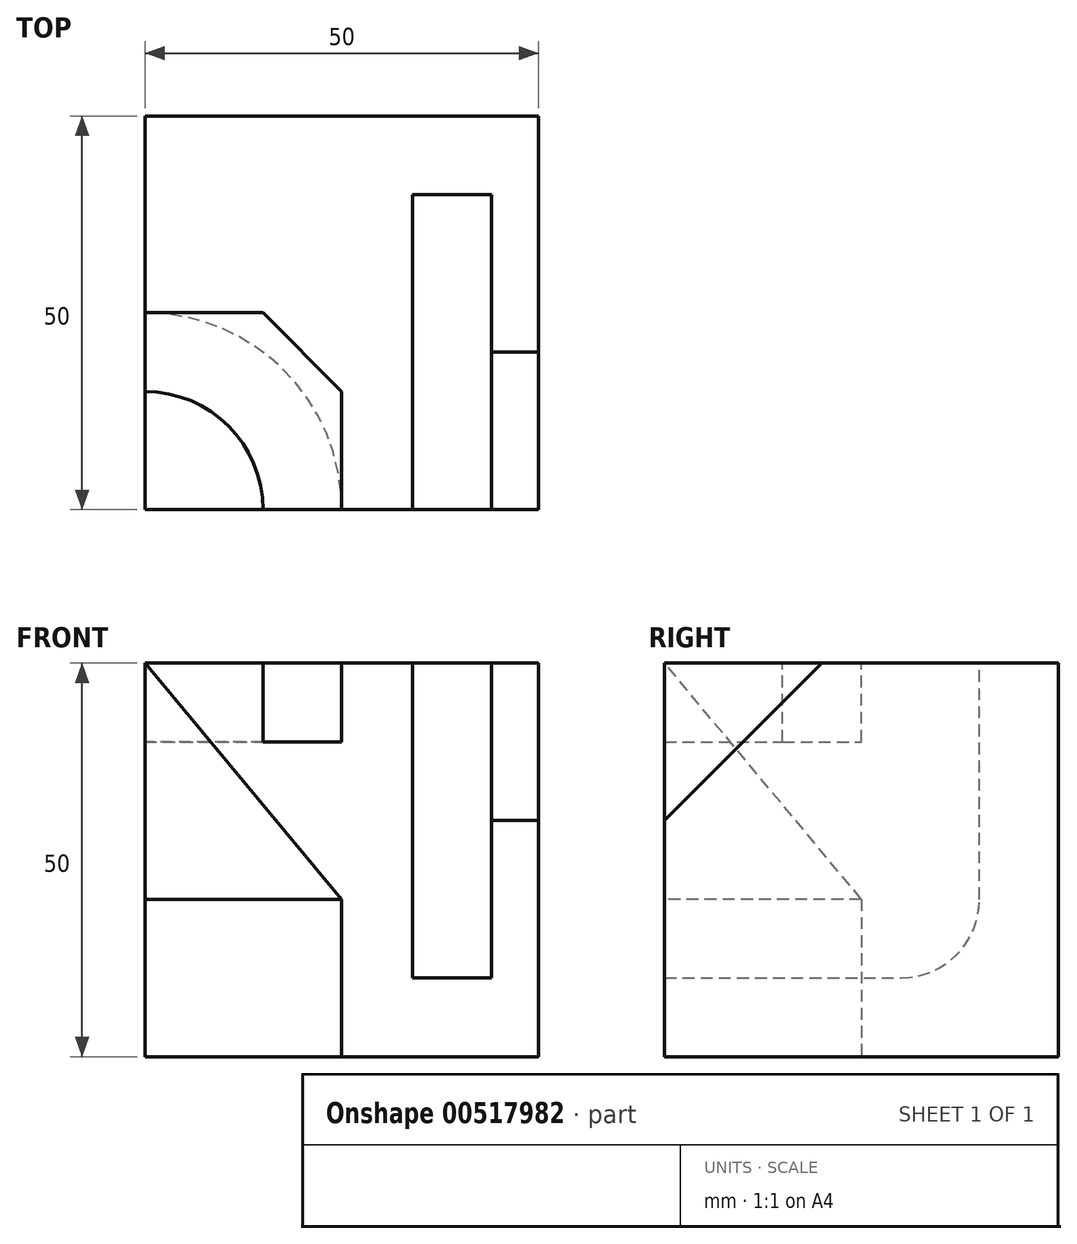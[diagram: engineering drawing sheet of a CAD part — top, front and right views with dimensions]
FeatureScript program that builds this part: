
annotation { "Feature Type Name" : "Feature", "Feature Type Description" : "" }
export const myFeature = defineFeature(function(context is Context, id is Id, definition is map)
    precondition{}
    {
        {
            var Q0;
            Q0=qCreatedBy(makeId("Top.planeOp"),FACE);
            var sketch = newSketch(context, id + "F0", { "sketchPlane" : qUnion([Q0])});
            skLineSegment(sketch, "E0.bottom", {"start": v(0, 0) * mm, "end": v(50, 0) * mm});
            skLineSegment(sketch, "E0.top", {"start": v(0, 50) * mm, "end": v(50, 50) * mm});
            skLineSegment(sketch, "E0.left", {"start": v(0, 0) * mm, "end": v(0, 50) * mm});
            skLineSegment(sketch, "E0.right", {"start": v(50, 0) * mm, "end": v(50, 50) * mm});
            skSolve(sketch);
        }
        {
            var Q0;
            Q0 = qSketchRegion(id + "F0", true);
            extrude(context, id + "F1", {"entities" : qUnion([Q0]), "depth" : 50 * mm, "offsetDistance" : 25 * mm});
        }
        {
            var Q0;
            Q0=makeQuery(id+"F1.opExtrude","CAP_FACE",FACE,{"disambiguationData":[OSD([sQuery(id+"F0.wireOp",EDGE,"E0.bottom"),sQuery(id+"F0.wireOp",EDGE,"E0.top"),sQuery(id+"F0.wireOp",EDGE,"E0.left"),sQuery(id+"F0.wireOp",EDGE,"E0.right")])],"isStart":false});
            var sketch = newSketch(context, id + "F2", { "sketchPlane" : qUnion([Q0])});
            skLineSegment(sketch, "E1.bottom", {"start": v(34, 0) * mm, "end": v(44, 0) * mm});
            skLineSegment(sketch, "E1.top", {"start": v(34, 40) * mm, "end": v(44, 40) * mm});
            skLineSegment(sketch, "E1.left", {"start": v(34, 0) * mm, "end": v(34, 40) * mm});
            skLineSegment(sketch, "E1.right", {"start": v(44, 0) * mm, "end": v(44, 40) * mm});
            skSolve(sketch);
        }
        {
            var Q0;
            Q0 = qSketchRegion(id + "F2", true);
            extrude(context, id + "F3", {"entities" : qUnion([Q0]), "operationType" : NewBodyOperationType.REMOVE, "oppositeDirection" : true, "depth" : 40 * mm, "offsetDistance" : 25 * mm});
        }
        {
            var Q0;
            Q0=makeQuery(id+"F1.opExtrude","SWEPT_FACE",FACE,{"disambiguationData":[OSD([sQuery(id+"F0.wireOp",EDGE,"E0.bottom")])]});
            var sketch = newSketch(context, id + "F4", { "sketchPlane" : qUnion([Q0])});
            skLineSegment(sketch, "E2", {"start": v(44, 30) * mm, "end": v(50, 30) * mm});
            skSolve(sketch);
        }
        {
            var Q0;
            Q0=makeQuery(id+"F1.opExtrude","SWEPT_FACE",FACE,{"disambiguationData":[OSD([sQuery(id+"F0.wireOp",EDGE,"E0.right")])]});
            var sketch = newSketch(context, id + "F5", { "sketchPlane" : qUnion([Q0])});
            skLineSegment(sketch, "E3", {"start": v(0, 30) * mm, "end": v(20, 50) * mm});
            skSolve(sketch);
        }
        {
            var Q0;
            Q0=makeQuery(id+"F3.boolean.opBoolean","COPY",EDGE,{"derivedFrom":makeQuery(id+"F3.opExtrude","CAP_EDGE",EDGE,{"disambiguationData":[OSD([sQuery(id+"F2.wireOp",EDGE,"E1.top")])],"isStart":false})});
            fillet(context, id + "F6", {"entities" : qUnion([Q0]), "radius" : 10 * mm, "tangentPropagation" : true, "allowEdgeOverflow" : false});
        }
        {
            var Q0;
            {var subQ0=sQuery(id+"F5.wireOp",EDGE,"E3");Q0=makeQuery(id+"F5.imprint","IMPRINT",FACE,{"disambiguationData":[TD([[makeQuery(id+"F5.imprint","IMPRINT",EDGE,{"derivedFrom":subQ0}),1.0]])]});}
            extrude(context, id + "F7", {"entities" : qUnion([Q0]), "operationType" : NewBodyOperationType.REMOVE, "oppositeDirection" : true, "depth" : 6 * mm, "offsetDistance" : 25 * mm});
        }
        {
            var Q0;
            Q0=makeQuery(id+"F1.opExtrude","CAP_FACE",FACE,{"disambiguationData":[OSD([sQuery(id+"F0.wireOp",EDGE,"E0.bottom"),sQuery(id+"F0.wireOp",EDGE,"E0.top"),sQuery(id+"F0.wireOp",EDGE,"E0.left"),sQuery(id+"F0.wireOp",EDGE,"E0.right")])],"isStart":true});
            var sketch = newSketch(context, id + "F8", { "sketchPlane" : qUnion([Q0])});
            skCircle(sketch, "E4", {"center": v(0, 0) * mm, "radius": 25 * mm});
            skSolve(sketch);
        }
        {
            var Q0;
            {var subQ0=sQuery(id+"F8.wireOp",EDGE,"E4");var subQ1=makeQuery(id+"F1.opExtrude","CAP_EDGE",EDGE,{"disambiguationData":[OSD([sQuery(id+"F0.wireOp",EDGE,"E0.bottom")])],"isStart":true});var subQ2=makeQuery(id+"F8.imprint","INTERSECT",VERTEX,{"derivedFrom":[subQ1,subQ0]});Q0=makeQuery(id+"F8.imprint","IMPRINT",FACE,{"disambiguationData":[TD([[makeQuery(id+"F8.imprint","IMPRINT",EDGE,{"disambiguationData":[TD([[subQ2,1.0]])],"derivedFrom":subQ0}),1.0]])]});}
            extrude(context, id + "F9", {"entities" : qUnion([Q0]), "operationType" : NewBodyOperationType.REMOVE, "oppositeDirection" : true, "depth" : 20 * mm, "offsetDistance" : 25 * mm});
        }
        {
            var Q0;
            {var subQ5=sQuery(id+"F4.wireOp",EDGE,"E2");Q0=makeQuery(id+"F4.imprint","IMPRINT",FACE,{"disambiguationData":[TD([[makeQuery(id+"F4.imprint","IMPRINT",EDGE,{"derivedFrom":subQ5}),-1.0]])]});}
            var sketch = newSketch(context, id + "F10", { "sketchPlane" : qUnion([Q0])});
            skLineSegment(sketch, "E5", {"start": v(0, 50) * mm, "end": v(25, 20) * mm});
            skSolve(sketch);
        }
        {
            var Q1;
            Q1=makeQuery(id+"F9.boolean.opBoolean","COPY",FACE,{"derivedFrom":makeQuery(id+"F9.opExtrude","CAP_FACE",FACE,{"disambiguationData":[OSD([sQuery(id+"F0.wireOp",EDGE,"E0.bottom"),sQuery(id+"F0.wireOp",EDGE,"E0.left"),sQuery(id+"F8.wireOp",EDGE,"E4")])],"isStart":false})});
            var Q2;
            Q2=sQuery(id+"F10.wireOp",VERTEX,"E5.start");
            loft(context, id + "F11", {"operationType" : NewBodyOperationType.REMOVE, "sheetProfilesArray" : [{ "sheetProfileEntities" : qUnion([Q1]) }, { "sheetProfileEntities" : qUnion([Q2]) }]});
        }
        {
            var Q0;
            Q0=makeQuery(id+"F1.opExtrude","CAP_FACE",FACE,{"disambiguationData":[OSD([sQuery(id+"F0.wireOp",EDGE,"E0.bottom"),sQuery(id+"F0.wireOp",EDGE,"E0.top"),sQuery(id+"F0.wireOp",EDGE,"E0.left"),sQuery(id+"F0.wireOp",EDGE,"E0.right")])],"isStart":false});
            var sketch = newSketch(context, id + "F12", { "sketchPlane" : qUnion([Q0])});
            skLineSegment(sketch, "E6.bottom", {"start": v(0, 0) * mm, "end": v(25, 0) * mm});
            skLineSegment(sketch, "E6.top", {"start": v(0, 25) * mm, "end": v(25, 25) * mm});
            skLineSegment(sketch, "E6.left", {"start": v(0, 0) * mm, "end": v(0, 25) * mm});
            skLineSegment(sketch, "E6.right", {"start": v(25, 0) * mm, "end": v(25, 25) * mm});
            skSolve(sketch);
        }
        {
            var Q0;
            {var subQ6=sQuery(id+"F12.wireOp",EDGE,"E6.top");Q0=makeQuery(id+"F12.imprint","IMPRINT",FACE,{"disambiguationData":[TD([[makeQuery(id+"F12.imprint","IMPRINT",EDGE,{"derivedFrom":subQ6}),-1.0]])]});}
            var sketch = newSketch(context, id + "F13", { "sketchPlane" : qUnion([Q0])});
            skCircle(sketch, "E7", {"center": v(0, 0) * mm, "radius": 15 * mm});
            skSolve(sketch);
        }
        {
            var Q0;
            {var subQ2=sQuery(id+"F12.wireOp",EDGE,"E6.top");var subQ3=makeQuery(id+"F12.imprint","IMPRINT",EDGE,{"derivedFrom":subQ2});Q0=makeQuery(id+"F13.imprint","IMPRINT",FACE,{"disambiguationData":[TD([[makeQuery(id+"F13.imprint","IMPRINT",EDGE,{"derivedFrom":subQ3}),-1.0]])]});}
            extrude(context, id + "F14", {"entities" : qUnion([Q0]), "operationType" : NewBodyOperationType.REMOVE, "oppositeDirection" : true, "depth" : 10 * mm, "offsetDistance" : 25 * mm});
        }
        {
            var Q0;
            Q0=makeQuery(id+"F14.boolean.opBoolean","COPY",EDGE,{"derivedFrom":makeQuery(id+"F14.opExtrude","SWEPT_EDGE",EDGE,{"disambiguationData":[OSD([sQuery(id+"F12.wireOp",EDGE,"E6.top"),sQuery(id+"F12.wireOp",EDGE,"E6.right")])]})});
            chamfer(context, id + "F15", {"entities" : qUnion([Q0]), "width" : 10 * mm, "tangentPropagation" : true});
        }
    });
